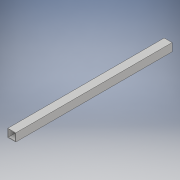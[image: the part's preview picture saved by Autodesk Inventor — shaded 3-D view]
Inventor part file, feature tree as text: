
AUTODESK INVENTOR PART (.ipt)
format: ipt  version: 2019.3 (Build 233278000, 278)  size: 101,376 bytes
history: native  units: mm
features: other x3, reference x2, extrude x1, sketch x1
ambient origin geometry x8: Origin, YZ Plane, XZ Plane, XY Plane, X Axis, Y Axis, Z Axis, Center Point
bodies: Solid1 (feature_tree)
feature tree (7):
  extrude  "Extrusion1"  Depth=22.225mm
  sketch  "Sketch1"  dims[d0=22.225mm d1=22.225mm d3=1.5875mm d8=500.0mm d9=0.0mm]
  reference  "Reference1"
  reference  "Reference2"
  parser-record x1  (decoder bookkeeping rows leaked as tree rows — omitted from the tree; the rows remain in map.json)
  other  "Assembly.iam"
  other  "RailMount:1"
note: 1 file-system path scrubbed to <path> (originals preserved in map.json)
